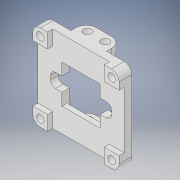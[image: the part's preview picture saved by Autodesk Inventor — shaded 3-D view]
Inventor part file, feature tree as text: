
AUTODESK INVENTOR PART (.ipt)
format: ipt  version: 2019 (Build 230136000, 136)  size: 292,352 bytes
history: native  units: mm
features: extrude x8, sketch x8, fillet x2, other x1
ambient origin geometry x8: Origin, YZ Plane, XZ Plane, XY Plane, X Axis, Y Axis, Z Axis, Center Point
bodies: Body1 (feature_tree)
feature tree (19):
  other  "솔리드1"
  extrude  "돌출1"  Depth=33.8mm
  extrude  "돌출2"  Depth=33.8mm
  extrude  "돌출3"  Depth=16.9mm
  extrude  "돌출4"  Depth=16.9mm
  extrude  "돌출5"  Depth=3.0mm TaperAngle=0.0deg
  fillet  "모깎기1"  Radius=2.5mm
  extrude  "돌출6"  Depth=2.5mm
  extrude  "돌출7"  Depth=2.5mm
  fillet  "모깎기2"  Radius=2.5mm
  extrude  "돌출10"  Depth=2.9mm
  sketch  "스케치1"
  sketch  "스케치2"
  sketch  "스케치3"
  sketch  "스케치4"
  sketch  "스케치5"
  sketch  "스케치6"
  sketch  "스케치7"
  sketch  "스케치10"
